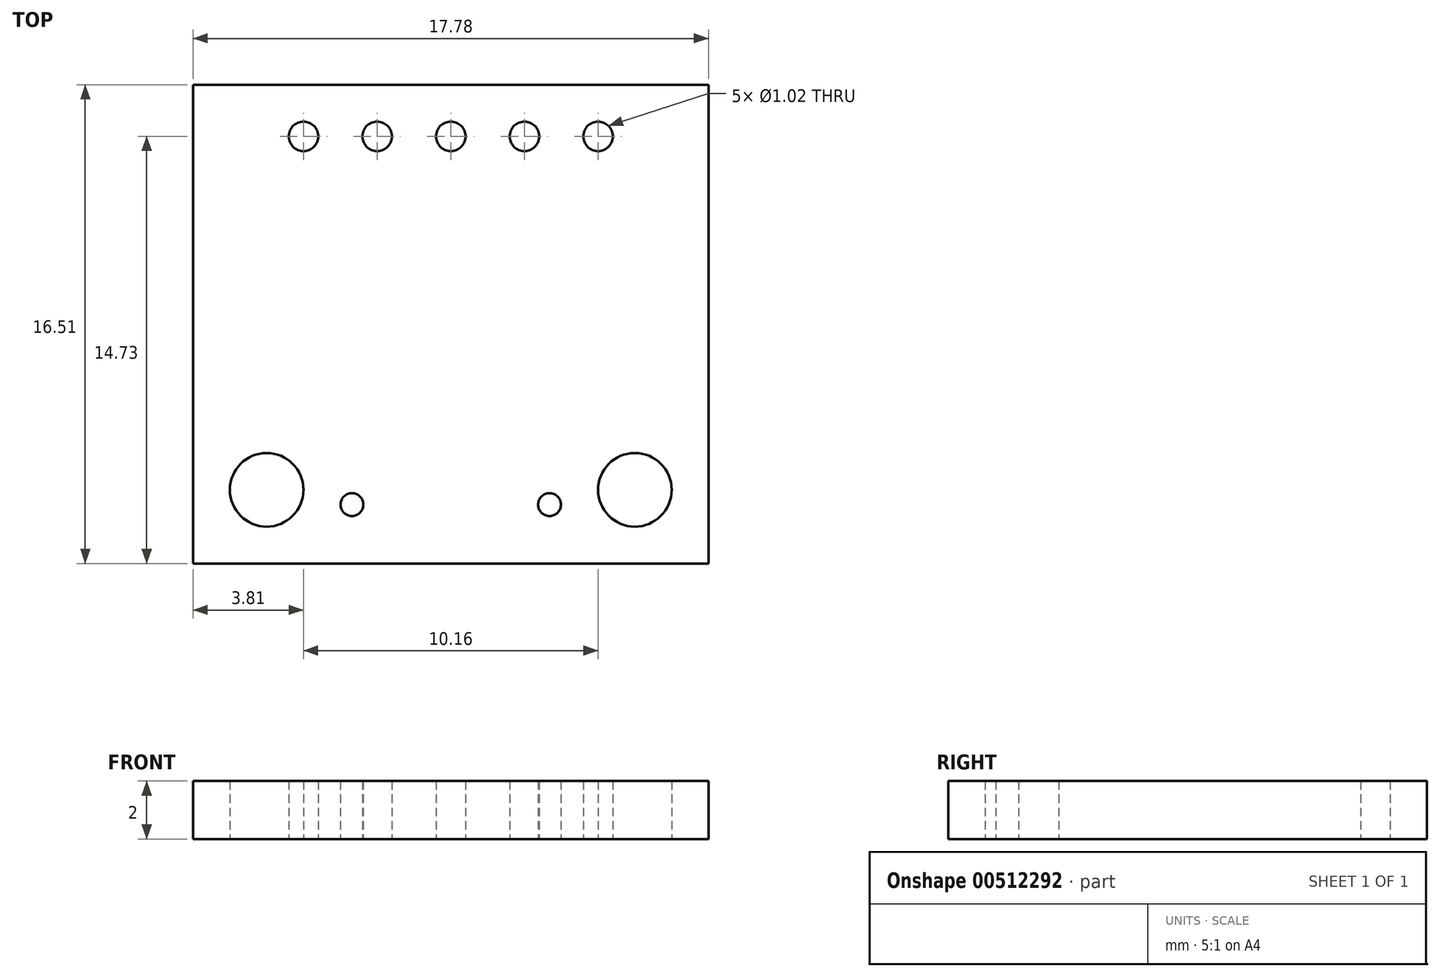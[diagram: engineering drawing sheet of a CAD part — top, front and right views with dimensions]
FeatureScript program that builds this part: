
annotation { "Feature Type Name" : "Feature", "Feature Type Description" : "" }
export const myFeature = defineFeature(function(context is Context, id is Id, definition is map)
    precondition{}
    {
        {
            var Q0;
            Q0=qCreatedBy(makeId("Top.planeOp"),FACE);
            var sketch = newSketch(context, id + "F0", { "sketchPlane" : qUnion([Q0])});
            skLineSegment(sketch, "E0.bottom", {"start": v(0, 0) * mm, "end": v(17.78, 0) * mm});
            skLineSegment(sketch, "E0.top", {"start": v(0, 16.51) * mm, "end": v(17.78, 16.51) * mm});
            skLineSegment(sketch, "E0.left", {"start": v(0, 0) * mm, "end": v(0, 16.51) * mm});
            skLineSegment(sketch, "E0.right", {"start": v(17.78, 0) * mm, "end": v(17.78, 16.51) * mm});
            skLineSegment(sketch, "E1", {"start": v(2.54, 2.54) * mm, "end": v(15.24, 2.54) * mm, "construction": true});
            skLineSegment(sketch, "E2", {"start": v(13.97, 14.73) * mm, "end": v(3.8, 14.73) * mm, "construction": true});
            skCircle(sketch, "E3", {"center": v(3.8, 14.73) * mm, "radius": 0.5 * mm});
            skCircle(sketch, "E4", {"center": v(6.35, 14.73) * mm, "radius": 0.5 * mm});
            skCircle(sketch, "E5", {"center": v(8.9, 14.73) * mm, "radius": 0.5 * mm});
            skCircle(sketch, "E6", {"center": v(11.43, 14.73) * mm, "radius": 0.5 * mm});
            skCircle(sketch, "E7", {"center": v(13.97, 14.73) * mm, "radius": 0.5 * mm});
            skCircle(sketch, "E8", {"center": v(2.54, 2.54) * mm, "radius": 1.27 * mm});
            skCircle(sketch, "E9", {"center": v(15.24, 2.54) * mm, "radius": 1.27 * mm});
            skLineSegment(sketch, "E10", {"start": v(8.9, 0) * mm, "end": v(8.9, 16.51) * mm, "construction": true});
            skCircle(sketch, "E11", {"center": v(5.48, 2.03) * mm, "radius": 0.4 * mm});
            skLineSegment(sketch, "E12", {"start": v(5.48, 2.03) * mm, "end": v(12.3, 2.03) * mm, "construction": true});
            skCircle(sketch, "E13", {"center": v(12.3, 2.03) * mm, "radius": 0.4 * mm});
            skSolve(sketch);
        }
        {
            var Q0;
            Q0 = qSketchRegion(id + "F0", true);
            extrude(context, id + "F1", {"entities" : qUnion([Q0]), "depth" : 2 * mm, "offsetDistance" : 25 * mm});
        }
    });
